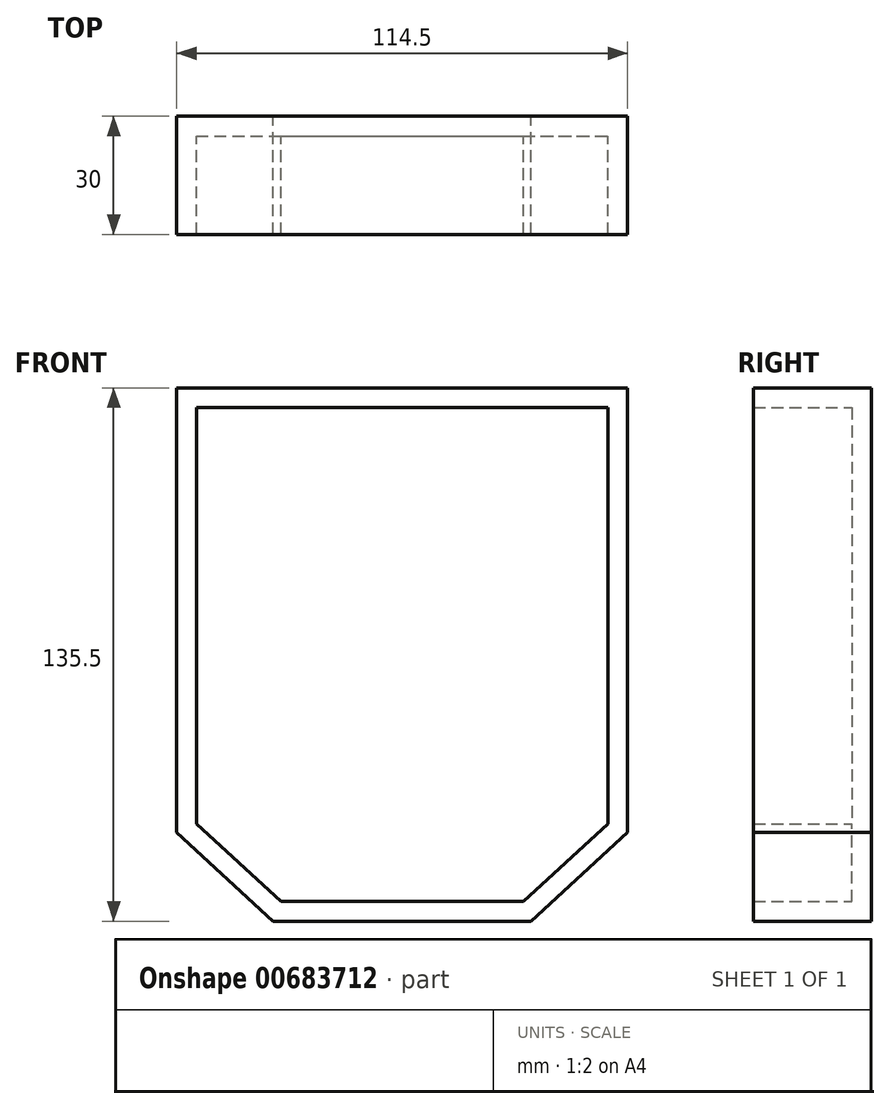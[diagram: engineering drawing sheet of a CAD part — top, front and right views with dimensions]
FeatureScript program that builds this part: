
annotation { "Feature Type Name" : "Feature", "Feature Type Description" : "" }
export const myFeature = defineFeature(function(context is Context, id is Id, definition is map)
    precondition{}
    {
        {
            var Q0;
            Q0=qCreatedBy(makeId("Front.planeOp"),FACE);
            var sketch = newSketch(context, id + "F0", { "sketchPlane" : qUnion([Q0])});
            skLineSegment(sketch, "E0.bottom", {"start": v(-66.45, 78.24) * mm, "end": v(48.05, 78.24) * mm});
            skLineSegment(sketch, "E0.top", {"start": v(-41.95, -57.26) * mm, "end": v(23.55, -57.26) * mm});
            skLineSegment(sketch, "E0.left", {"start": v(-66.45, 78.24) * mm, "end": v(-66.45, -34.76) * mm});
            skLineSegment(sketch, "E0.right", {"start": v(48.05, 78.24) * mm, "end": v(48.05, -34.76) * mm});
            skLineSegment(sketch, "E1", {"start": v(-66.45, -34.76) * mm, "end": v(-41.95, -57.26) * mm});
            skLineSegment(sketch, "E2", {"start": v(23.55, -57.26) * mm, "end": v(48.05, -34.76) * mm});
            skSolve(sketch);
        }
        {
            var Q0;
            Q0 = qSketchRegion(id + "F0", true);
            extrude(context, id + "F1", {"entities" : qUnion([Q0]), "depth" : 5 * mm, "offsetDistance" : 25 * mm});
        }
        {
            var Q0;
            Q0=makeQuery(id+"F1.opExtrude","CAP_FACE",FACE,{"disambiguationData":[OSD([sQuery(id+"F0.wireOp",EDGE,"E0.bottom"),sQuery(id+"F0.wireOp",EDGE,"E0.top"),sQuery(id+"F0.wireOp",EDGE,"E0.left"),sQuery(id+"F0.wireOp",EDGE,"E0.right"),sQuery(id+"F0.wireOp",EDGE,"E1"),sQuery(id+"F0.wireOp",EDGE,"E2")])],"isStart":false});
            var sketch = newSketch(context, id + "F2", { "sketchPlane" : qUnion([Q0])});
            skLineSegment(sketch, "E3.0", {"start": v(-61.45, 73.24) * mm, "end": v(-61.45, -32.56) * mm});
            skLineSegment(sketch, "E3.1", {"start": v(43.05, 73.24) * mm, "end": v(43.05, -32.56) * mm});
            skLineSegment(sketch, "E3.2", {"start": v(21.6, -52.26) * mm, "end": v(43.05, -32.56) * mm});
            skLineSegment(sketch, "E3.3", {"start": v(-61.45, 73.24) * mm, "end": v(43.05, 73.24) * mm});
            skLineSegment(sketch, "E3.4", {"start": v(-40, -52.26) * mm, "end": v(21.6, -52.26) * mm});
            skLineSegment(sketch, "E3.5", {"start": v(-61.45, -32.56) * mm, "end": v(-40, -52.26) * mm});
            skSolve(sketch);
        }
        {
            var Q0;
            Q0=makeQuery(id+"F2.imprint","IMPRINT",FACE,{"disambiguationData":[TD([[makeQuery(id+"F2.imprint","IMPRINT",EDGE,{"derivedFrom":sQuery(id+"F2.wireOp",EDGE,"E3.0")}),-1.0]])]});
            extrude(context, id + "F3", {"entities" : qUnion([Q0]), "operationType" : NewBodyOperationType.ADD, "depth" : 25 * mm, "offsetDistance" : 25 * mm});
        }
    });
